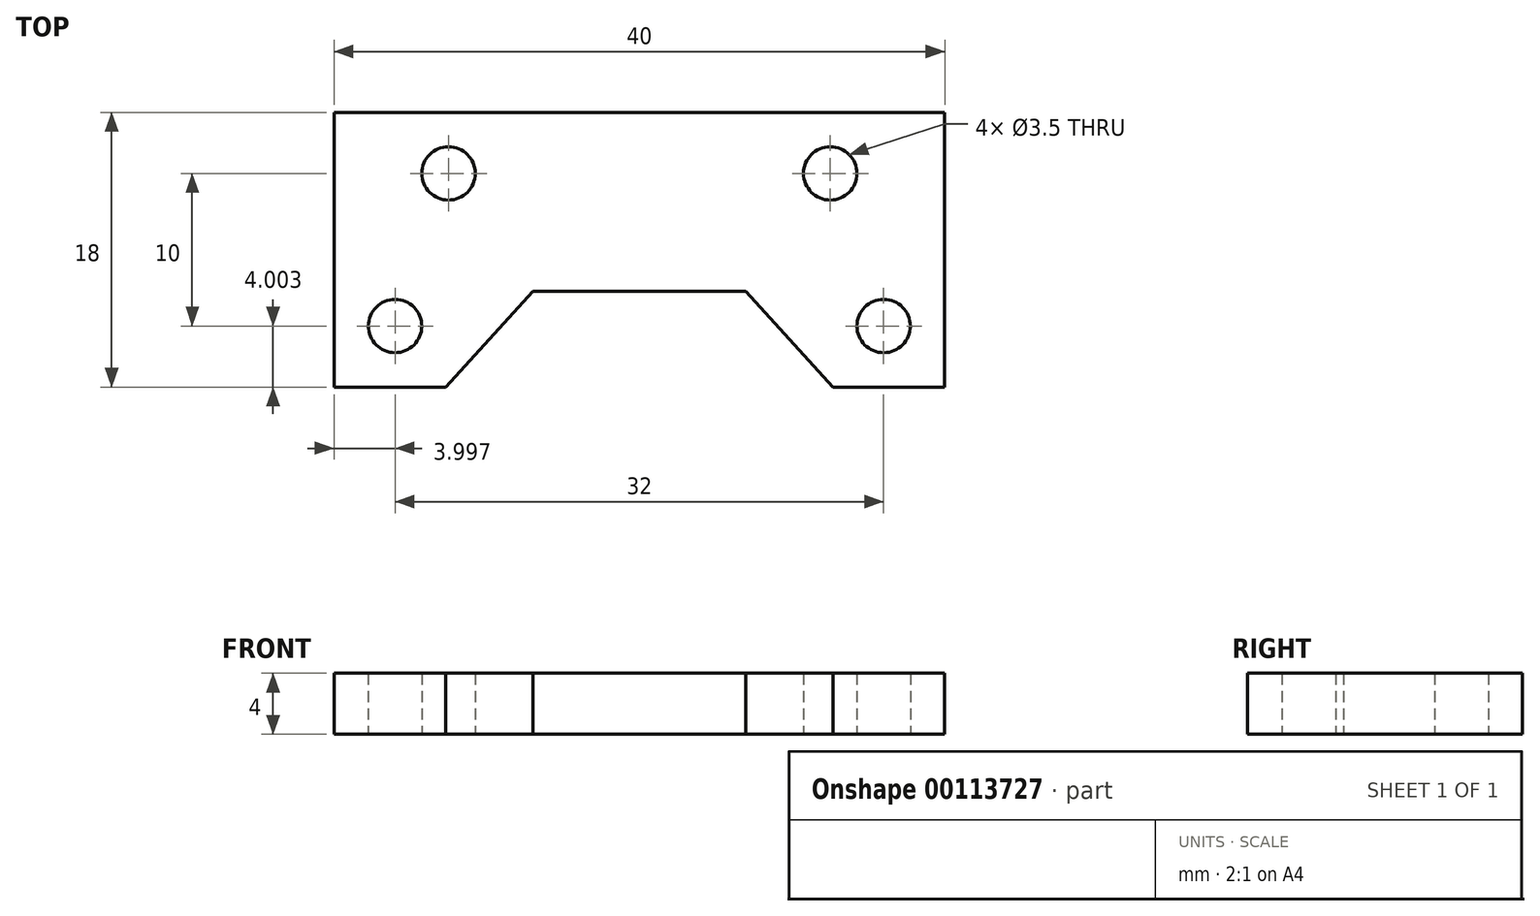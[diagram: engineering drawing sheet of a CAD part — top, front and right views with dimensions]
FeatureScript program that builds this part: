
annotation { "Feature Type Name" : "Feature", "Feature Type Description" : "" }
export const myFeature = defineFeature(function(context is Context, id is Id, definition is map)
    precondition{}
    {
        {
            var Q0;
            Q0=qCreatedBy(makeId("Top.planeOp"),FACE);
            var sketch = newSketch(context, id + "F0", { "sketchPlane" : qUnion([Q0])});
            skLineSegment(sketch, "E0.bottom", {"start": v(3.23, 3.35) * mm, "end": v(43.23, 3.35) * mm});
            skLineSegment(sketch, "E0.top", {"start": v(3.23, -14.65) * mm, "end": v(43.23, -14.65) * mm});
            skLineSegment(sketch, "E0.left", {"start": v(3.23, 3.35) * mm, "end": v(3.23, -14.65) * mm});
            skLineSegment(sketch, "E0.right", {"start": v(43.23, 3.35) * mm, "end": v(43.23, -14.65) * mm});
            skLineSegment(sketch, "E1", {"start": v(23.23, -14.65) * mm, "end": v(23.23, 3.35) * mm});
            skLineSegment(sketch, "E2", {"start": v(10.55, -14.65) * mm, "end": v(16.26, -8.38) * mm});
            skLineSegment(sketch, "E3", {"start": v(16.26, -8.38) * mm, "end": v(23.23, -8.38) * mm});
            skLineSegment(sketch, "E4.MirrorCS", {"start": v(30.2, -8.38) * mm, "end": v(23.23, -8.38) * mm});
            skLineSegment(sketch, "E5.MirrorCS", {"start": v(35.9, -14.65) * mm, "end": v(30.2, -8.38) * mm});
            skCircle(sketch, "E6", {"center": v(10.73, -0.65) * mm, "radius": 1.75 * mm});
            skCircle(sketch, "E7.1.0.0", {"center": v(35.73, -0.65) * mm, "radius": 1.75 * mm});
            skLineSegment(sketch, "E7.direction1", {"start": v(10.73, -0.65) * mm, "end": v(35.73, -0.65) * mm, "construction": true});
            skCircle(sketch, "E8", {"center": v(7.23, -10.65) * mm, "radius": 1.75 * mm});
            skCircle(sketch, "E9.1.0.0", {"center": v(39.23, -10.65) * mm, "radius": 1.75 * mm});
            skLineSegment(sketch, "E9.direction1", {"start": v(7.23, -10.65) * mm, "end": v(39.23, -10.65) * mm, "construction": true});
            skSolve(sketch);
        }
        {
            var Q0;
            {var subQ4=sQuery(id+"F0.wireOp",EDGE,"E0.left");Q0=makeQuery(id+"F0.imprint","IMPRINT",FACE,{"disambiguationData":[TD([[makeQuery(id+"F0.imprint","IMPRINT",EDGE,{"derivedFrom":subQ4}),1.0]])]});}
            var Q1;
            {var subQ4=sQuery(id+"F0.wireOp",EDGE,"E0.right");Q1=makeQuery(id+"F0.imprint","IMPRINT",FACE,{"disambiguationData":[TD([[makeQuery(id+"F0.imprint","IMPRINT",EDGE,{"derivedFrom":subQ4}),-1.0]])]});}
            extrude(context, id + "F1", {"entities" : qUnion([Q0, Q1]), "depth" : 4 * mm});
        }
    });
